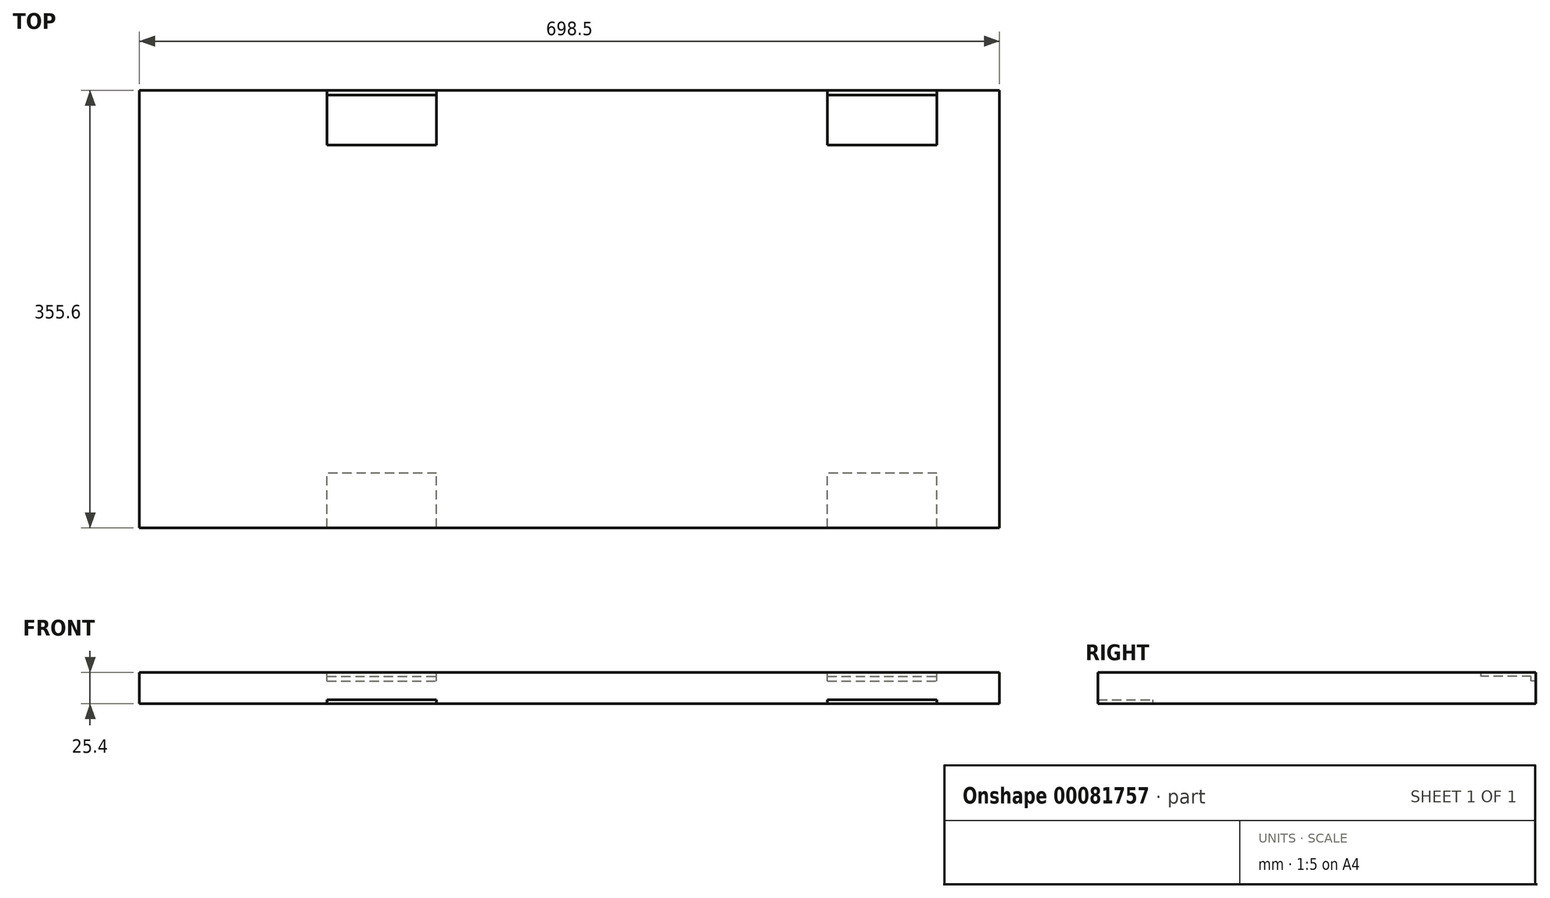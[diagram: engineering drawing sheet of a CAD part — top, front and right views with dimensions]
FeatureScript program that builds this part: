
annotation { "Feature Type Name" : "Feature", "Feature Type Description" : "" }
export const myFeature = defineFeature(function(context is Context, id is Id, definition is map)
    precondition{}
    {
        {
            var Q0;
            Q0=qCreatedBy(makeId("Top.planeOp"),FACE);
            var sketch = newSketch(context, id + "F0", { "sketchPlane" : qUnion([Q0])});
            skLineSegment(sketch, "E0.bottom", {"start": v(-349.25, -177.8) * mm, "end": v(349.25, -177.8) * mm});
            skLineSegment(sketch, "E0.top", {"start": v(-349.25, 177.8) * mm, "end": v(349.25, 177.8) * mm});
            skLineSegment(sketch, "E0.left", {"start": v(-349.25, -177.8) * mm, "end": v(-349.25, 177.8) * mm});
            skLineSegment(sketch, "E0.right", {"start": v(349.25, -177.8) * mm, "end": v(349.25, 177.8) * mm});
            skPoint(sketch, "E0.middle", {"position": v(0, 0) * mm});
            skSolve(sketch);
        }
        {
            var Q0;
            Q0=makeQuery(id+"F0.imprint","IMPRINT",FACE,{"disambiguationData":[TD([[makeQuery(id+"F0.imprint","IMPRINT",EDGE,{"derivedFrom":sQuery(id+"F0.wireOp",EDGE,"E0.bottom")}),1.0]])]});
            extrude(context, id + "F1", {"entities" : qUnion([Q0]), "depth" : 25.4 * mm});
        }
        {
            var Q0;
            Q0=makeQuery(id+"F1.opExtrude","CAP_FACE",FACE,{"disambiguationData":[OSD([sQuery(id+"F0.wireOp",EDGE,"E0.bottom"),sQuery(id+"F0.wireOp",EDGE,"E0.top"),sQuery(id+"F0.wireOp",EDGE,"E0.left"),sQuery(id+"F0.wireOp",EDGE,"E0.right")])],"isStart":false});
            var sketch = newSketch(context, id + "F2", { "sketchPlane" : qUnion([Q0])});
            skLineSegment(sketch, "E1.bottom", {"start": v(-196.85, 177.8) * mm, "end": v(-107.95, 177.8) * mm});
            skLineSegment(sketch, "E1.top", {"start": v(-196.85, 133.35) * mm, "end": v(-107.95, 133.35) * mm});
            skLineSegment(sketch, "E1.left", {"start": v(-196.85, 177.8) * mm, "end": v(-196.85, 133.35) * mm});
            skLineSegment(sketch, "E1.right", {"start": v(-107.95, 177.8) * mm, "end": v(-107.95, 133.35) * mm});
            skLineSegment(sketch, "E2.bottom", {"start": v(209.55, 177.8) * mm, "end": v(298.45, 177.8) * mm});
            skLineSegment(sketch, "E2.top", {"start": v(209.55, 133.35) * mm, "end": v(298.45, 133.35) * mm});
            skLineSegment(sketch, "E2.left", {"start": v(209.55, 177.8) * mm, "end": v(209.55, 133.35) * mm});
            skLineSegment(sketch, "E2.right", {"start": v(298.45, 177.8) * mm, "end": v(298.45, 133.35) * mm});
            skSolve(sketch);
        }
        {
            var Q0;
            Q0 = qSketchRegion(id + "F2", true);
            extrude(context, id + "F3", {"entities" : qUnion([Q0]), "operationType" : NewBodyOperationType.REMOVE, "oppositeDirection" : true, "depth" : 3.17 * mm});
        }
        {
            var Q0;
            Q0=makeQuery(id+"F1.opExtrude","CAP_FACE",FACE,{"disambiguationData":[OSD([sQuery(id+"F0.wireOp",EDGE,"E0.bottom"),sQuery(id+"F0.wireOp",EDGE,"E0.top"),sQuery(id+"F0.wireOp",EDGE,"E0.left"),sQuery(id+"F0.wireOp",EDGE,"E0.right")])],"isStart":true});
            var sketch = newSketch(context, id + "F4", { "sketchPlane" : qUnion([Q0])});
            skLineSegment(sketch, "E3.bottom", {"start": v(298.45, 177.8) * mm, "end": v(209.55, 177.8) * mm});
            skLineSegment(sketch, "E3.top", {"start": v(298.45, 133.35) * mm, "end": v(209.55, 133.35) * mm});
            skLineSegment(sketch, "E3.left", {"start": v(298.45, 177.8) * mm, "end": v(298.45, 133.35) * mm});
            skLineSegment(sketch, "E3.right", {"start": v(209.55, 177.8) * mm, "end": v(209.55, 133.35) * mm});
            skLineSegment(sketch, "E4.bottom", {"start": v(-107.95, 177.8) * mm, "end": v(-196.85, 177.8) * mm});
            skLineSegment(sketch, "E4.top", {"start": v(-107.95, 133.35) * mm, "end": v(-196.85, 133.35) * mm});
            skLineSegment(sketch, "E4.left", {"start": v(-107.95, 177.8) * mm, "end": v(-107.95, 133.35) * mm});
            skLineSegment(sketch, "E4.right", {"start": v(-196.85, 177.8) * mm, "end": v(-196.85, 133.35) * mm});
            skSolve(sketch);
        }
        {
            var Q0;
            Q0 = qSketchRegion(id + "F4", true);
            extrude(context, id + "F5", {"entities" : qUnion([Q0]), "operationType" : NewBodyOperationType.REMOVE, "oppositeDirection" : true, "depth" : 3.17 * mm});
        }
        {
            var Q0;
            Q0=makeQuery(id+"F3.boolean.opBoolean","COPY",FACE,{"derivedFrom":makeQuery(id+"F3.opExtrude","CAP_FACE",FACE,{"disambiguationData":[OSD([sQuery(id+"F2.wireOp",EDGE,"E1.bottom"),sQuery(id+"F2.wireOp",EDGE,"E1.top"),sQuery(id+"F2.wireOp",EDGE,"E1.left"),sQuery(id+"F2.wireOp",EDGE,"E1.right")])],"isStart":false})});
            var sketch = newSketch(context, id + "F6", { "sketchPlane" : qUnion([Q0])});
            skLineSegment(sketch, "E5.bottom", {"start": v(-196.85, 177.8) * mm, "end": v(-107.95, 177.8) * mm});
            skLineSegment(sketch, "E5.top", {"start": v(-196.85, 174) * mm, "end": v(-107.95, 174) * mm});
            skLineSegment(sketch, "E5.left", {"start": v(-196.85, 177.8) * mm, "end": v(-196.85, 174) * mm});
            skLineSegment(sketch, "E5.right", {"start": v(-107.95, 177.8) * mm, "end": v(-107.95, 174) * mm});
            skSolve(sketch);
        }
        {
            var Q0;
            Q0 = qSketchRegion(id + "F6", true);
            extrude(context, id + "F7", {"entities" : qUnion([Q0]), "operationType" : NewBodyOperationType.REMOVE, "oppositeDirection" : true, "depth" : 3.8 * mm});
        }
        {
            var Q0;
            Q0=makeQuery(id+"F3.boolean.opBoolean","COPY",FACE,{"derivedFrom":makeQuery(id+"F3.opExtrude","CAP_FACE",FACE,{"disambiguationData":[OSD([sQuery(id+"F2.wireOp",EDGE,"E2.bottom"),sQuery(id+"F2.wireOp",EDGE,"E2.top"),sQuery(id+"F2.wireOp",EDGE,"E2.left"),sQuery(id+"F2.wireOp",EDGE,"E2.right")])],"isStart":false})});
            var sketch = newSketch(context, id + "F8", { "sketchPlane" : qUnion([Q0])});
            skLineSegment(sketch, "E6.bottom", {"start": v(209.55, 177.8) * mm, "end": v(298.45, 177.8) * mm});
            skLineSegment(sketch, "E6.top", {"start": v(209.55, 174) * mm, "end": v(298.45, 174) * mm});
            skLineSegment(sketch, "E6.left", {"start": v(209.55, 177.8) * mm, "end": v(209.55, 174) * mm});
            skLineSegment(sketch, "E6.right", {"start": v(298.45, 177.8) * mm, "end": v(298.45, 174) * mm});
            skSolve(sketch);
        }
        {
            var Q0;
            Q0 = qSketchRegion(id + "F8", true);
            extrude(context, id + "F9", {"entities" : qUnion([Q0]), "operationType" : NewBodyOperationType.REMOVE, "oppositeDirection" : true, "depth" : 3.8 * mm});
        }
    });
